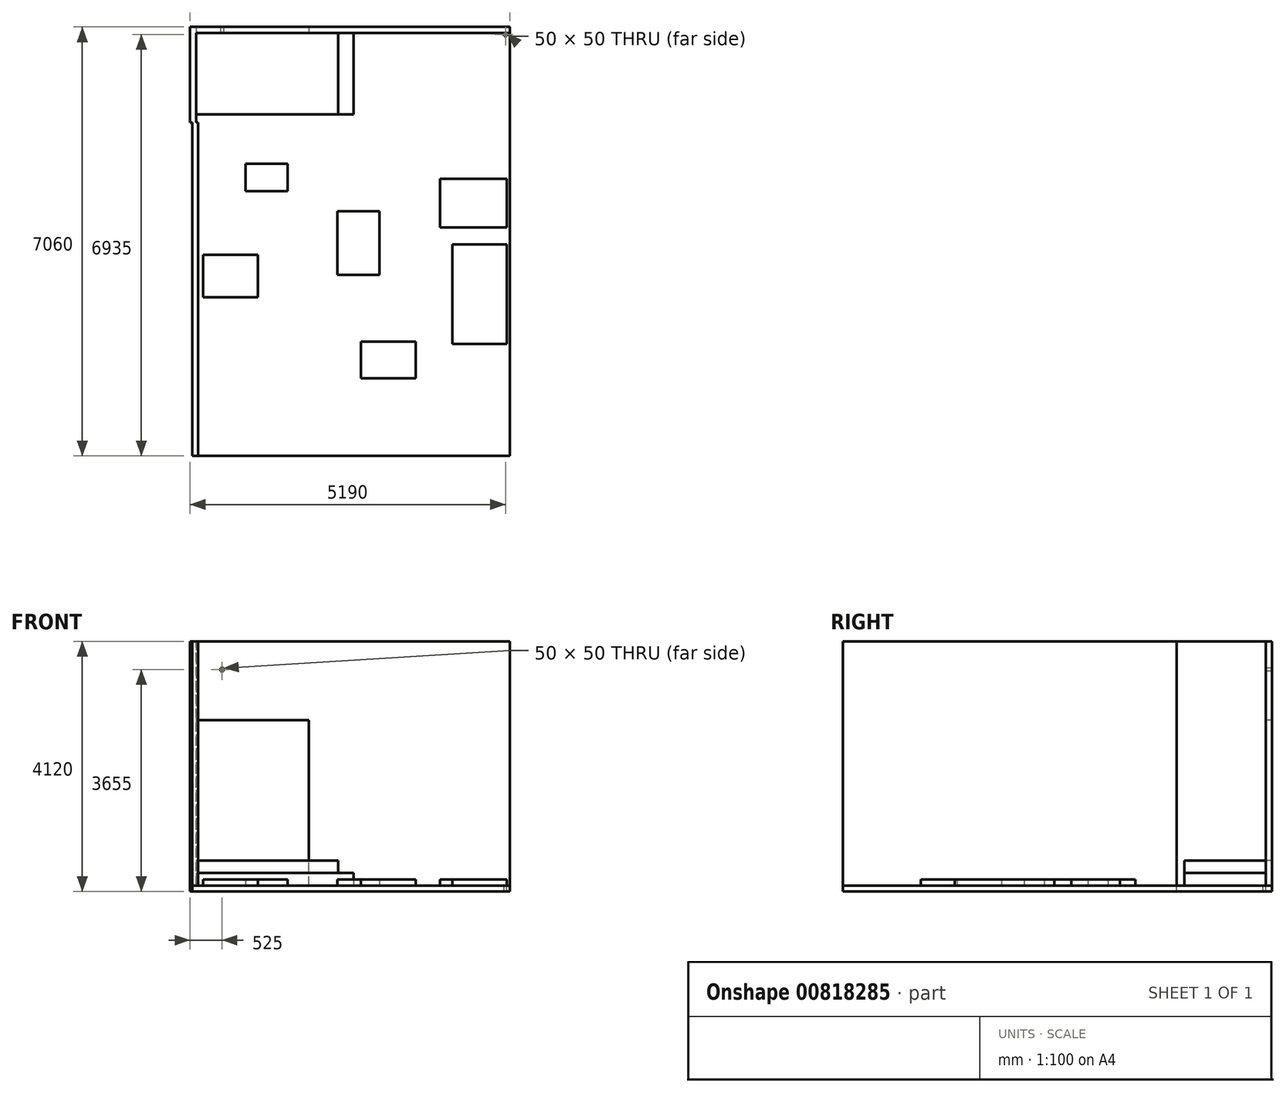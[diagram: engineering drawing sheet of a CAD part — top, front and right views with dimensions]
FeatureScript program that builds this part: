
annotation { "Feature Type Name" : "Feature", "Feature Type Description" : "" }
export const myFeature = defineFeature(function(context is Context, id is Id, definition is map)
    precondition{}
    {
        {
            var Q0;
            Q0=qCreatedBy(makeId("Right.planeOp"),FACE);
            var sketch = newSketch(context, id + "F0", { "sketchPlane" : qUnion([Q0])});
            skLineSegment(sketch, "E0.bottom", {"start": v(-2745, 2010) * mm, "end": v(2745, 2010) * mm});
            skLineSegment(sketch, "E0.top", {"start": v(-2745, -2010) * mm, "end": v(2745, -2010) * mm});
            skLineSegment(sketch, "E0.left", {"start": v(-2745, 2010) * mm, "end": v(-2745, -2010) * mm});
            skLineSegment(sketch, "E0.right", {"start": v(2745, 2010) * mm, "end": v(2745, -2010) * mm});
            skPoint(sketch, "E0.middle", {"position": v(0, 0) * mm});
            skSolve(sketch);
        }
        {
            var Q0;
            Q0 = qSketchRegion(id + "F0", true);
            extrude(context, id + "F1", {"entities" : qUnion([Q0]), "oppositeDirection" : true, "depth" : 100 * mm, "offsetDistance" : 25 * mm});
        }
        {
            var Q0;
            Q0=makeQuery(id+"F1.opExtrude","CAP_FACE",FACE,{"disambiguationData":[OSD([sQuery(id+"F0.wireOp",EDGE,"E0.bottom"),sQuery(id+"F0.wireOp",EDGE,"E0.top"),sQuery(id+"F0.wireOp",EDGE,"E0.left"),sQuery(id+"F0.wireOp",EDGE,"E0.right")])],"isStart":true});
            cPlane(context, id + "F2", {"entities" : qUnion([Q0]), "cplaneType" : CPlaneType.OFFSET, "offset" : 35 * mm, "oppositeDirection" : true, "width" : 150 * mm, "height" : 150 * mm});
        }
        {
            var Q0;
            Q0=qCreatedBy(id+"F2.planeOp",FACE);
            var sketch = newSketch(context, id + "F3", { "sketchPlane" : qUnion([Q0])});
            skPoint(sketch, "E1.0", {"position": v(2745, 2010) * mm});
            skLineSegment(sketch, "E2", {"start": v(2745, 2010) * mm, "end": v(4215, 2010) * mm});
            skLineSegment(sketch, "E3", {"start": v(4215, 2010) * mm, "end": v(4215, -2010) * mm});
            skLineSegment(sketch, "E4", {"start": v(4215, -2010) * mm, "end": v(2745, -2010) * mm});
            skLineSegment(sketch, "E5", {"start": v(2745, -2010) * mm, "end": v(2745, 2010) * mm});
            skSolve(sketch);
        }
        {
            var Q0;
            Q0 = qSketchRegion(id + "F3", true);
            extrude(context, id + "F4", {"entities" : qUnion([Q0]), "operationType" : NewBodyOperationType.ADD, "oppositeDirection" : true, "depth" : 100 * mm, "offsetDistance" : 25 * mm});
        }
        {
            var Q0;
            Q0=qCreatedBy(makeId("Front.planeOp"),FACE);
            cPlane(context, id + "F5", {"entities" : qUnion([Q0]), "cplaneType" : CPlaneType.OFFSET, "offset" : 4215 * mm, "oppositeDirection" : true, "width" : 150 * mm, "height" : 150 * mm});
        }
        {
            var Q0;
            Q0=qCreatedBy(id+"F5.planeOp",FACE);
            var sketch = newSketch(context, id + "F6", { "sketchPlane" : qUnion([Q0])});
            skLineSegment(sketch, "E6.0", {"start": v(-35, 2010) * mm, "end": v(-35, -2010) * mm});
            skLineSegment(sketch, "E7", {"start": v(-35, 2010) * mm, "end": v(5130, 2010) * mm});
            skLineSegment(sketch, "E8", {"start": v(5130, 2010) * mm, "end": v(5130, -2010) * mm});
            skLineSegment(sketch, "E9", {"start": v(5130, -2010) * mm, "end": v(-35, -2010) * mm});
            skLineSegment(sketch, "E10", {"start": v(-35, -2010) * mm, "end": v(-135, -2010) * mm});
            skLineSegment(sketch, "E11", {"start": v(-135, -2010) * mm, "end": v(-135, 2010) * mm});
            skLineSegment(sketch, "E12", {"start": v(-135, 2010) * mm, "end": v(-35, 2010) * mm});
            skLineSegment(sketch, "E13", {"start": v(-35, 710) * mm, "end": v(1820, 710) * mm});
            skLineSegment(sketch, "E14", {"start": v(1820, 710) * mm, "end": v(1820, -2010) * mm});
            skSolve(sketch);
        }
        {
            var Q0;
            Q0 = qSketchRegion(id + "F6", true);
            extrude(context, id + "F7", {"entities" : qUnion([Q0]), "operationType" : NewBodyOperationType.ADD, "oppositeDirection" : true, "depth" : 100 * mm, "offsetDistance" : 25 * mm});
        }
        {
            var Q0;
            Q0=makeQuery(id+"F7.opExtrude","CAP_FACE",FACE,{"disambiguationData":[OSD([sQuery(id+"F6.wireOp",EDGE,"E7"),sQuery(id+"F6.wireOp",EDGE,"E8"),sQuery(id+"F6.wireOp",EDGE,"E9"),sQuery(id+"F6.wireOp",EDGE,"E10"),sQuery(id+"F6.wireOp",EDGE,"E11"),sQuery(id+"F6.wireOp",EDGE,"E12")])],"isStart":true});
            var sketch = newSketch(context, id + "F8", { "sketchPlane" : qUnion([Q0])});
            skLineSegment(sketch, "E15.0", {"start": v(-35, 710) * mm, "end": v(1820, 710) * mm});
            skLineSegment(sketch, "E16.0", {"start": v(1820, 710) * mm, "end": v(1820, -2010) * mm});
            skLineSegment(sketch, "E17", {"start": v(-35, 710) * mm, "end": v(-35, -2010) * mm});
            skLineSegment(sketch, "E18", {"start": v(-35, -2010) * mm, "end": v(1820, -2010) * mm});
            skSolve(sketch);
        }
        {
            var Q0;
            Q0 = qSketchRegion(id + "F8", true);
            extrude(context, id + "F9", {"entities" : qUnion([Q0]), "operationType" : NewBodyOperationType.REMOVE, "oppositeDirection" : true, "depth" : 100 * mm, "offsetDistance" : 25 * mm});
        }
        {
            var Q0;
            Q0=qCreatedBy(makeId("Top.planeOp"),FACE);
            cPlane(context, id + "F10", {"entities" : qUnion([Q0]), "cplaneType" : CPlaneType.OFFSET, "offset" : 2010 * mm, "oppositeDirection" : true, "width" : 150 * mm, "height" : 150 * mm});
        }
        {
            var Q0;
            Q0=qCreatedBy(id+"F10.planeOp",FACE);
            var sketch = newSketch(context, id + "F11", { "sketchPlane" : qUnion([Q0])});
            skLineSegment(sketch, "E19.0", {"start": v(-100, -2745) * mm, "end": v(-100, 2745) * mm});
            skLineSegment(sketch, "E20.0", {"start": v(-135, 2745) * mm, "end": v(-100, 2745) * mm});
            skLineSegment(sketch, "E21.0", {"start": v(-135, 4315) * mm, "end": v(-135, 2745) * mm});
            skLineSegment(sketch, "E22.0", {"start": v(-35, 4315) * mm, "end": v(1820, 4315) * mm});
            skLineSegment(sketch, "E23.0", {"start": v(5130, 4315) * mm, "end": v(1820, 4315) * mm});
            skLineSegment(sketch, "E24.0", {"start": v(5130, 4315) * mm, "end": v(5130, 4215) * mm});
            skLineSegment(sketch, "E25.0", {"start": v(-100, -2745) * mm, "end": v(0, -2745) * mm});
            skLineSegment(sketch, "E26.0", {"start": v(-35, 4315) * mm, "end": v(-135, 4315) * mm});
            skLineSegment(sketch, "E27", {"start": v(0, -2745) * mm, "end": v(5130, -2745) * mm});
            skLineSegment(sketch, "E28", {"start": v(5130, 4215) * mm, "end": v(5130, -2745) * mm});
            skSolve(sketch);
        }
        {
            var Q0;
            Q0 = qSketchRegion(id + "F11", true);
            extrude(context, id + "F12", {"entities" : qUnion([Q0]), "oppositeDirection" : true, "depth" : 100 * mm, "offsetDistance" : 25 * mm});
        }
        {
            var Q0;
            Q0=makeQuery(id+"F12.opExtrude","CAP_FACE",FACE,{"disambiguationData":[OSD([sQuery(id+"F11.wireOp",EDGE,"E19.0"),sQuery(id+"F11.wireOp",EDGE,"E20.0"),sQuery(id+"F11.wireOp",EDGE,"E21.0"),sQuery(id+"F11.wireOp",EDGE,"E22.0"),sQuery(id+"F11.wireOp",EDGE,"E23.0"),sQuery(id+"F11.wireOp",EDGE,"E24.0"),sQuery(id+"F11.wireOp",EDGE,"E25.0"),sQuery(id+"F11.wireOp",EDGE,"E26.0"),sQuery(id+"F11.wireOp",EDGE,"E27"),sQuery(id+"F11.wireOp",EDGE,"E28")])],"isStart":true});
            var sketch = newSketch(context, id + "F13", { "sketchPlane" : qUnion([Q0])});
            skPoint(sketch, "E29.0", {"position": v(5130, 4215) * mm});
            skLineSegment(sketch, "E30", {"start": v(5130, 4215) * mm, "end": v(5130, 1815) * mm, "construction": true});
            skLineSegment(sketch, "E31", {"start": v(5080, 1815) * mm, "end": v(3980, 1815) * mm});
            skLineSegment(sketch, "E32", {"start": v(3980, 1815) * mm, "end": v(3980, 1015) * mm});
            skLineSegment(sketch, "E33", {"start": v(3980, 1015) * mm, "end": v(5080, 1015) * mm});
            skLineSegment(sketch, "E34", {"start": v(5130, 1015) * mm, "end": v(5130, 735) * mm, "construction": true});
            skLineSegment(sketch, "E35", {"start": v(5080, 735) * mm, "end": v(4180, 735) * mm});
            skLineSegment(sketch, "E36", {"start": v(4180, 735) * mm, "end": v(4180, -905) * mm});
            skLineSegment(sketch, "E37", {"start": v(4180, -905) * mm, "end": v(5080, -905) * mm});
            skLineSegment(sketch, "E38", {"start": v(3580, -2745) * mm, "end": v(3580, -1465) * mm, "construction": true});
            skLineSegment(sketch, "E39", {"start": v(3580, -1465) * mm, "end": v(3580, -865) * mm});
            skLineSegment(sketch, "E40", {"start": v(3580, -865) * mm, "end": v(2680, -865) * mm});
            skLineSegment(sketch, "E41", {"start": v(2680, -865) * mm, "end": v(2680, -1465) * mm});
            skLineSegment(sketch, "E42", {"start": v(2680, -1465) * mm, "end": v(3580, -1465) * mm});
            skLineSegment(sketch, "E43", {"start": v(2980, -2745) * mm, "end": v(2980, 235) * mm, "construction": true});
            skLineSegment(sketch, "E44", {"start": v(2980, 235) * mm, "end": v(2980, 1285) * mm});
            skLineSegment(sketch, "E45", {"start": v(2980, 1285) * mm, "end": v(2290, 1285) * mm});
            skLineSegment(sketch, "E46", {"start": v(2290, 1285) * mm, "end": v(2290, 235) * mm});
            skLineSegment(sketch, "E47", {"start": v(2290, 235) * mm, "end": v(2980, 235) * mm});
            skLineSegment(sketch, "E48", {"start": v(5080, -905) * mm, "end": v(5080, 735) * mm});
            skLineSegment(sketch, "E49", {"start": v(5080, 1015) * mm, "end": v(5080, 1815) * mm});
            skPoint(sketch, "E50.orphan", {"position": v(5130, -905) * mm});
            skLineSegment(sketch, "E51", {"start": v(80, -135) * mm, "end": v(80, 565) * mm});
            skLineSegment(sketch, "E52", {"start": v(80, 565) * mm, "end": v(980, 565) * mm});
            skLineSegment(sketch, "E53", {"start": v(980, 565) * mm, "end": v(980, -135) * mm});
            skLineSegment(sketch, "E54", {"start": v(980, -135) * mm, "end": v(80, -135) * mm});
            skLineSegment(sketch, "E55", {"start": v(780, 1615) * mm, "end": v(1470, 1615) * mm});
            skLineSegment(sketch, "E56", {"start": v(1470, 1615) * mm, "end": v(1470, 2065) * mm});
            skLineSegment(sketch, "E57", {"start": v(1470, 2065) * mm, "end": v(780, 2065) * mm});
            skLineSegment(sketch, "E58", {"start": v(780, 2065) * mm, "end": v(780, 1615) * mm});
            skSolve(sketch);
        }
        {
            var Q0;
            Q0 = qSketchRegion(id + "F13", true);
            extrude(context, id + "F14", {"entities" : qUnion([Q0]), "operationType" : NewBodyOperationType.ADD, "depth" : 100 * mm, "offsetDistance" : 25 * mm});
        }
        {
            var Q0;
            Q0=makeQuery(id+"F12.opExtrude","CAP_FACE",FACE,{"disambiguationData":[OSD([sQuery(id+"F11.wireOp",EDGE,"E19.0"),sQuery(id+"F11.wireOp",EDGE,"E20.0"),sQuery(id+"F11.wireOp",EDGE,"E21.0"),sQuery(id+"F11.wireOp",EDGE,"E22.0"),sQuery(id+"F11.wireOp",EDGE,"E23.0"),sQuery(id+"F11.wireOp",EDGE,"E24.0"),sQuery(id+"F11.wireOp",EDGE,"E25.0"),sQuery(id+"F11.wireOp",EDGE,"E26.0"),sQuery(id+"F11.wireOp",EDGE,"E27"),sQuery(id+"F11.wireOp",EDGE,"E28")])],"isStart":true});
            var sketch = newSketch(context, id + "F15", { "sketchPlane" : qUnion([Q0])});
            skPoint(sketch, "E59.0", {"position": v(-35, 4215) * mm});
            skPoint(sketch, "E60.orphan", {"position": v(-35, 4315) * mm});
            skLineSegment(sketch, "E61", {"start": v(-35, 2875) * mm, "end": v(2555, 2875) * mm});
            skLineSegment(sketch, "E62", {"start": v(2555, 2875) * mm, "end": v(2555, 4215) * mm});
            skLineSegment(sketch, "E63", {"start": v(-35, 2875) * mm, "end": v(-35, 4215) * mm});
            skLineSegment(sketch, "E64", {"start": v(-35, 4215) * mm, "end": v(2555, 4215) * mm});
            skSolve(sketch);
        }
        {
            var Q0;
            Q0 = qSketchRegion(id + "F15", true);
            extrude(context, id + "F16", {"entities" : qUnion([Q0]), "depth" : 210 * mm, "offsetDistance" : 25 * mm});
        }
        {
            var Q0;
            Q0=makeQuery(id+"F16.opExtrude","CAP_FACE",FACE,{"disambiguationData":[OSD([sQuery(id+"F15.wireOp",EDGE,"E61"),sQuery(id+"F15.wireOp",EDGE,"E62"),sQuery(id+"F15.wireOp",EDGE,"E63"),sQuery(id+"F15.wireOp",EDGE,"E64")])],"isStart":false});
            var sketch = newSketch(context, id + "F17", { "sketchPlane" : qUnion([Q0])});
            skLineSegment(sketch, "E65.0", {"start": v(-35, 2875) * mm, "end": v(-35, 4215) * mm});
            skLineSegment(sketch, "E66", {"start": v(-35, 2875) * mm, "end": v(2305, 2875) * mm});
            skLineSegment(sketch, "E67", {"start": v(2305, 2875) * mm, "end": v(2305, 4215) * mm});
            skLineSegment(sketch, "E68", {"start": v(2305, 4215) * mm, "end": v(-35, 4215) * mm});
            skSolve(sketch);
        }
        {
            var Q0;
            Q0 = qSketchRegion(id + "F17", true);
            extrude(context, id + "F18", {"entities" : qUnion([Q0]), "depth" : 200 * mm, "offsetDistance" : 25 * mm});
        }
        {
            var Q0;
            Q0=makeQuery(id+"F18.opExtrude","CAP_FACE",FACE,{"disambiguationData":[OSD([sQuery(id+"F17.wireOp",EDGE,"E65.0"),sQuery(id+"F17.wireOp",EDGE,"E66"),sQuery(id+"F17.wireOp",EDGE,"E67"),sQuery(id+"F17.wireOp",EDGE,"E68")])],"isStart":false});
            var sketch = newSketch(context, id + "F19", { "sketchPlane" : qUnion([Q0])});
            skPoint(sketch, "E69.0", {"position": v(1820, 4215) * mm});
            skPoint(sketch, "E70.0", {"position": v(-35, 4215) * mm});
            skLineSegment(sketch, "E71", {"start": v(-35, 4215) * mm, "end": v(1820, 4215) * mm});
            skLineSegment(sketch, "E72", {"start": v(1820, 4315) * mm, "end": v(-35, 4315) * mm});
            skLineSegment(sketch, "E73", {"start": v(-35, 4315) * mm, "end": v(-35, 4215) * mm});
            skLineSegment(sketch, "E74", {"start": v(1820, 4315) * mm, "end": v(1820, 4215) * mm});
            skSolve(sketch);
        }
        {
            var Q0;
            Q0 = qSketchRegion(id + "F19", true);
            extrude(context, id + "F20", {"entities" : qUnion([Q0]), "oppositeDirection" : true, "depth" : 510 * mm, "offsetDistance" : 25 * mm});
        }
        {
            var Q0;
            Q0=makeQuery(id+"F12.opExtrude","SWEPT_BODY",BODY,{"disambiguationData":[OSD([sQuery(id+"F11.wireOp",EDGE,"E19.0"),sQuery(id+"F11.wireOp",EDGE,"E20.0"),sQuery(id+"F11.wireOp",EDGE,"E21.0"),sQuery(id+"F11.wireOp",EDGE,"E22.0"),sQuery(id+"F11.wireOp",EDGE,"E23.0"),sQuery(id+"F11.wireOp",EDGE,"E24.0"),sQuery(id+"F11.wireOp",EDGE,"E25.0"),sQuery(id+"F11.wireOp",EDGE,"E26.0"),sQuery(id+"F11.wireOp",EDGE,"E27"),sQuery(id+"F11.wireOp",EDGE,"E28")])]});
            var Q1;
            Q1=makeQuery(id+"F20.opExtrude","SWEPT_BODY",BODY,{"disambiguationData":[OSD([sQuery(id+"F19.wireOp",EDGE,"E71"),sQuery(id+"F19.wireOp",EDGE,"E72"),sQuery(id+"F19.wireOp",EDGE,"E73"),sQuery(id+"F19.wireOp",EDGE,"E74")])]});
            booleanBodies(context, id + "F21", {"operationType" : BooleanOperationType.UNION, "tools" : qUnion([Q0, Q1])});
        }
        {
            var Q0;
            Q0=makeQuery(id+"F1.opExtrude","CAP_FACE",FACE,{"disambiguationData":[OSD([sQuery(id+"F0.wireOp",EDGE,"E0.bottom"),sQuery(id+"F0.wireOp",EDGE,"E0.top"),sQuery(id+"F0.wireOp",EDGE,"E0.left"),sQuery(id+"F0.wireOp",EDGE,"E0.right")])],"isStart":true});
            var sketch = newSketch(context, id + "F22", { "sketchPlane" : qUnion([Q0])});
            skLineSegment(sketch, "E75.0", {"start": v(4315, -2010) * mm, "end": v(-2745, -2010) * mm, "construction": true});
            skLineSegment(sketch, "E76", {"start": v(-2745, -590) * mm, "end": v(-405, -590) * mm, "construction": true});
            skLineSegment(sketch, "E77", {"start": v(-405, -590) * mm, "end": v(-405, -540) * mm, "construction": true});
            skLineSegment(sketch, "E78", {"start": v(-405, -540) * mm, "end": v(-2745, -540) * mm, "construction": true});
            skLineSegment(sketch, "E79", {"start": v(-2745, -540) * mm, "end": v(-2745, -590) * mm, "construction": true});
            skSolve(sketch);
        }
        {
            var Q0;
            Q0=makeQuery(id+"F12.opExtrude","CAP_FACE",FACE,{"disambiguationData":[OSD([sQuery(id+"F11.wireOp",EDGE,"E19.0"),sQuery(id+"F11.wireOp",EDGE,"E20.0"),sQuery(id+"F11.wireOp",EDGE,"E21.0"),sQuery(id+"F11.wireOp",EDGE,"E22.0"),sQuery(id+"F11.wireOp",EDGE,"E23.0"),sQuery(id+"F11.wireOp",EDGE,"E24.0"),sQuery(id+"F11.wireOp",EDGE,"E25.0"),sQuery(id+"F11.wireOp",EDGE,"E26.0"),sQuery(id+"F11.wireOp",EDGE,"E27"),sQuery(id+"F11.wireOp",EDGE,"E28")])],"isStart":true});
            var sketch = newSketch(context, id + "F23", { "sketchPlane" : qUnion([Q0])});
            skPoint(sketch, "E80.0", {"position": v(5130, 4215) * mm});
            skLineSegment(sketch, "E81", {"start": v(5130, 4215) * mm, "end": v(5080, 4215) * mm, "construction": true});
            skLineSegment(sketch, "E82.bottom", {"start": v(5080, 4215) * mm, "end": v(5030, 4215) * mm});
            skLineSegment(sketch, "E82.top", {"start": v(5080, 4165) * mm, "end": v(5030, 4165) * mm});
            skLineSegment(sketch, "E82.left", {"start": v(5080, 4215) * mm, "end": v(5080, 4165) * mm});
            skLineSegment(sketch, "E82.right", {"start": v(5030, 4215) * mm, "end": v(5030, 4165) * mm});
            skSolve(sketch);
        }
        {
            var Q0;
            Q0 = qSketchRegion(id + "F23", true);
            extrude(context, id + "F24", {"entities" : qUnion([Q0]), "operationType" : NewBodyOperationType.REMOVE, "oppositeDirection" : true, "depth" : 100 * mm, "offsetDistance" : 25 * mm});
        }
        {
            var Q0;
            Q0=makeQuery(id+"F7.opExtrude","CAP_FACE",FACE,{"disambiguationData":[OSD([sQuery(id+"F6.wireOp",EDGE,"E7"),sQuery(id+"F6.wireOp",EDGE,"E8"),sQuery(id+"F6.wireOp",EDGE,"E9"),sQuery(id+"F6.wireOp",EDGE,"E10"),sQuery(id+"F6.wireOp",EDGE,"E11"),sQuery(id+"F6.wireOp",EDGE,"E12")])],"isStart":true});
            var sketch = newSketch(context, id + "F25", { "sketchPlane" : qUnion([Q0])});
            skLineSegment(sketch, "E83.bottom", {"start": v(365, 1570) * mm, "end": v(415, 1570) * mm});
            skLineSegment(sketch, "E83.top", {"start": v(365, 1520) * mm, "end": v(415, 1520) * mm});
            skLineSegment(sketch, "E83.left", {"start": v(365, 1570) * mm, "end": v(365, 1520) * mm});
            skLineSegment(sketch, "E83.right", {"start": v(415, 1570) * mm, "end": v(415, 1520) * mm});
            skLineSegment(sketch, "E84.0", {"start": v(-35, -1600) * mm, "end": v(2305, -1600) * mm, "construction": true});
            skLineSegment(sketch, "E85.0", {"start": v(-35, 2010) * mm, "end": v(-35, 710) * mm, "construction": true});
            skSolve(sketch);
        }
        {
            var Q0;
            Q0 = qSketchRegion(id + "F25", true);
            extrude(context, id + "F26", {"entities" : qUnion([Q0]), "operationType" : NewBodyOperationType.REMOVE, "oppositeDirection" : true, "depth" : 100 * mm, "offsetDistance" : 25 * mm});
        }
        {
            var Q0;
            Q0=makeQuery(id+"F22.imprint","IMPRINT",FACE,{"disambiguationData":[TD([[makeQuery(id+"F22.imprint","IMPRINT",EDGE,{"derivedFrom":makeQuery(id+"F1.opExtrude","CAP_EDGE",EDGE,{"disambiguationData":[OSD([sQuery(id+"F0.wireOp",EDGE,"E0.bottom")])],"isStart":true})}),-1.0]])]});
            var sketch = newSketch(context, id + "F27", { "sketchPlane" : qUnion([Q0])});
            skLineSegment(sketch, "E86.0", {"start": v(-2745, 2010) * mm, "end": v(-2745, -2010) * mm, "construction": true});
            skLineSegment(sketch, "E87", {"start": v(-2745, -1090) * mm, "end": v(1180, -1090) * mm, "construction": true});
            skSolve(sketch);
        }
    });
